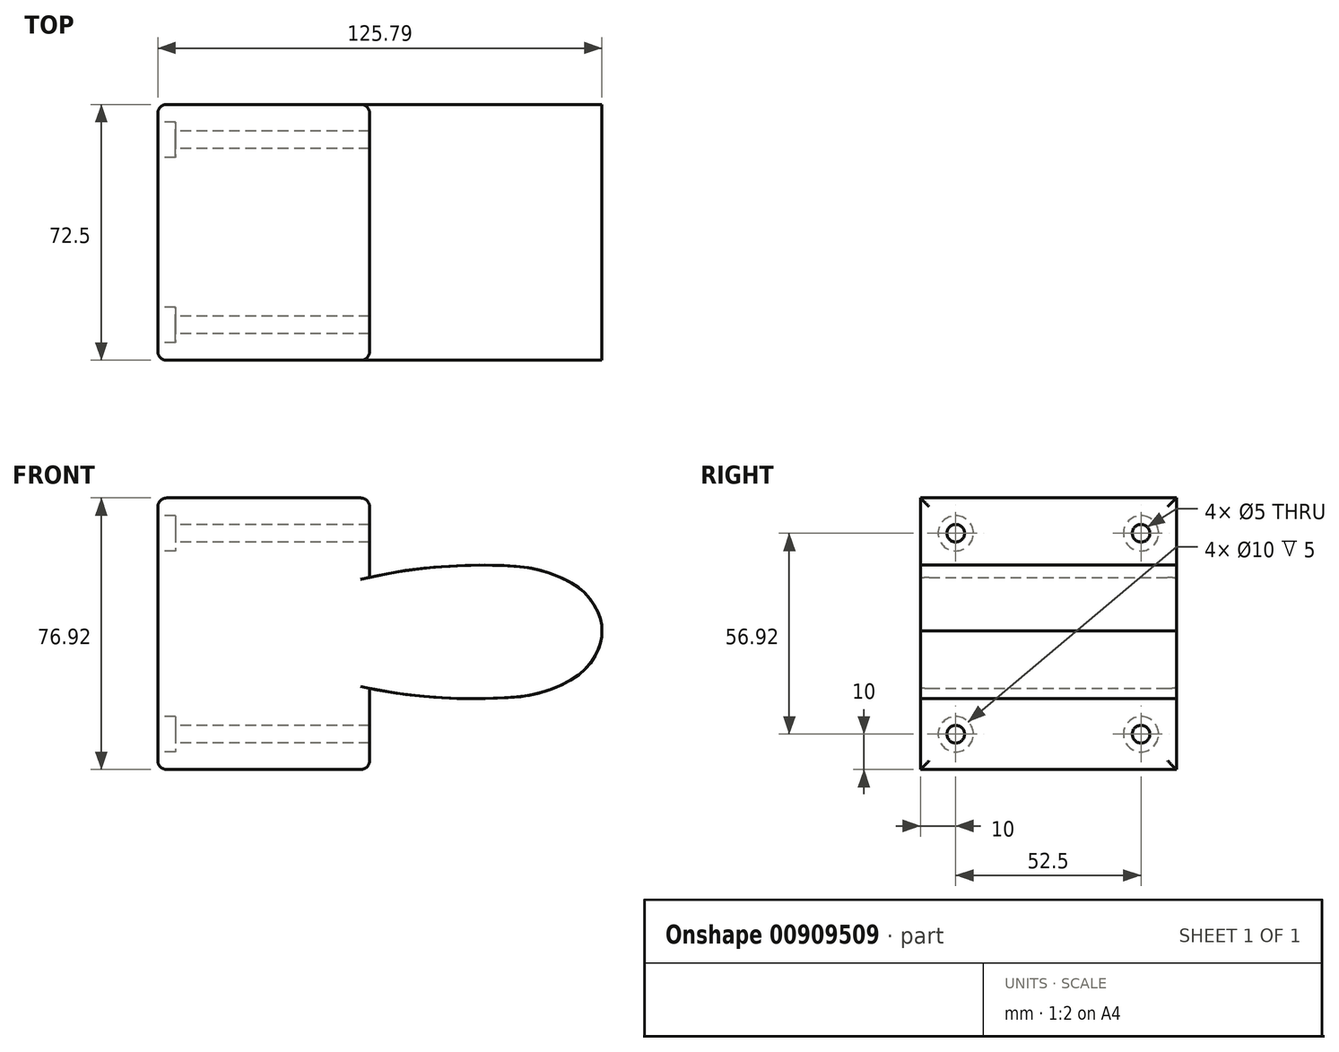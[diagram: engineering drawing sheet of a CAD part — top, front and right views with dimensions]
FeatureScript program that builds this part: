
annotation { "Feature Type Name" : "Feature", "Feature Type Description" : "" }
export const myFeature = defineFeature(function(context is Context, id is Id, definition is map)
    precondition{}
    {
        {
            var Q0;
            Q0=qCreatedBy(makeId("Front.planeOp"),FACE);
            var sketch = newSketch(context, id + "F0", { "sketchPlane" : qUnion([Q0])});
            skFitSpline(sketch, "E0.0", {"points": [v(-56.59, 0.04) * mm, v(-55.54, 0.85) * mm, v(-53.18, 2.44) * mm, v(-49, 4.79) * mm, v(-44.32, 7.05) * mm, v(-39.28, 9.2) * mm, v(-34.03, 11.2) * mm, v(-29.6, 12.7) * mm, v(-26.1, 13.78) * mm, v(-22.66, 14.76) * mm, v(-18.46, 15.83) * mm, v(-13.6, 16.88) * mm, v(-7.4, 18) * mm, v(-1.56, 18.74) * mm, v(3.83, 19.2) * mm, v(7.67, 19.44) * mm, v(11.33, 19.58) * mm, v(14.83, 19.62) * mm, v(17.61, 19.6) * mm, v(19.78, 19.56) * mm, v(21.92, 19.49) * mm, v(24.55, 19.33) * mm, v(27.14, 19.04) * mm, v(29.2, 18.69) * mm, v(30.73, 18.36) * mm, v(32.25, 17.95) * mm, v(34.23, 17.33) * mm, v(36.6, 16.42) * mm, v(38.75, 15.39) * mm, v(40.3, 14.52) * mm, v(41.36, 13.85) * mm, v(42.34, 13.16) * mm, v(43.26, 12.42) * mm, v(44.1, 11.62) * mm, v(44.9, 10.76) * mm, v(45.63, 9.83) * mm, v(46.32, 8.84) * mm, v(46.96, 7.8) * mm, v(47.53, 6.73) * mm, v(47.93, 5.84) * mm, v(48.2, 5.12) * mm, v(48.38, 4.58) * mm, v(48.52, 4.05) * mm, v(48.66, 3.37) * mm, v(48.77, 2.58) * mm, v(48.81, 1.73) * mm, v(48.82, 1.25) * mm, v(48.83, 1.03) * mm]});
            skFitSpline(sketch, "E0.1", {"points": [v(-56.59, 0.04) * mm, v(-55.52, -0.74) * mm, v(-53.13, -2.3) * mm, v(-48.9, -4.56) * mm, v(-44.19, -6.73) * mm, v(-39.1, -8.8) * mm, v(-33.82, -10.69) * mm, v(-29.36, -12.1) * mm, v(-25.85, -13.11) * mm, v(-22.38, -14.03) * mm, v(-18.17, -15.02) * mm, v(-13.3, -15.98) * mm, v(-7.06, -16.98) * mm, v(-1.22, -17.6) * mm, v(4.19, -17.98) * mm, v(8.03, -18.14) * mm, v(11.7, -18.2) * mm, v(15.19, -18.18) * mm, v(17.97, -18.1) * mm, v(20.13, -18.02) * mm, v(22.27, -17.91) * mm, v(24.9, -17.7) * mm, v(27.49, -17.36) * mm, v(29.54, -16.97) * mm, v(31.06, -16.62) * mm, v(32.57, -16.18) * mm, v(34.54, -15.52) * mm, v(36.9, -14.56) * mm, v(39.02, -13.5) * mm, v(40.55, -12.6) * mm, v(41.6, -11.9) * mm, v(42.58, -11.2) * mm, v(43.48, -10.44) * mm, v(44.3, -9.62) * mm, v(45.08, -8.75) * mm, v(45.8, -7.8) * mm, v(46.47, -6.8) * mm, v(47.09, -5.75) * mm, v(47.64, -4.67) * mm, v(48.02, -3.77) * mm, v(48.28, -3.05) * mm, v(48.45, -2.5) * mm, v(48.58, -1.97) * mm, v(48.7, -1.29) * mm, v(48.8, -0.5) * mm, v(48.83, 0.35) * mm, v(48.83, 0.83) * mm, v(48.83, 1.06) * mm]});
            skLineSegment(sketch, "E1", {"start": v(-16.96, 16.14) * mm, "end": v(-16.96, 38.67) * mm});
            skLineSegment(sketch, "E2", {"start": v(-16.96, 38.67) * mm, "end": v(-76.96, 38.67) * mm});
            skLineSegment(sketch, "E3", {"start": v(-76.96, 38.67) * mm, "end": v(-76.96, -38.25) * mm});
            skLineSegment(sketch, "E4", {"start": v(-76.96, -38.25) * mm, "end": v(-16.96, -38.25) * mm});
            skLineSegment(sketch, "E5", {"start": v(-16.96, -38.25) * mm, "end": v(-16.96, -15.25) * mm});
            skSolve(sketch);
        }
        {
            var Q0;
            Q0=qSketchRegion(id+"F0",true);
            extrude(context, id + "F1", {"entities" : qUnion([Q0]), "depth" : 72.5 * mm, "offsetDistance" : 25 * mm});
        }
        {
            var Q0;
            Q0=makeQuery(id+"F1.opExtrude","SWEPT_FACE",FACE,{"disambiguationData":[OSD([sQuery(id+"F0.wireOp",EDGE,"E3")])]});
            var sketch = newSketch(context, id + "F2", { "sketchPlane" : qUnion([Q0])});
            skLineSegment(sketch, "E6", {"start": v(10, 64.3) * mm, "end": v(10, -67.48) * mm, "construction": true});
            skLineSegment(sketch, "E7", {"start": v(62.5, 65.18) * mm, "end": v(62.5, -67.48) * mm, "construction": true});
            skLineSegment(sketch, "E8", {"start": v(-71.51, -28.25) * mm, "end": v(121.85, -28.25) * mm, "construction": true});
            skLineSegment(sketch, "E9", {"start": v(-71.51, 28.67) * mm, "end": v(123.4, 28.67) * mm, "construction": true});
            skPoint(sketch, "E10", {"position": v(10, 28.67) * mm});
            skPoint(sketch, "E11", {"position": v(62.5, 28.67) * mm});
            skPoint(sketch, "E12", {"position": v(62.5, -28.25) * mm});
            skPoint(sketch, "E13", {"position": v(10, -28.25) * mm});
            skSolve(sketch);
        }
        {
            var Q0;
            Q0=sQuery(id+"F2.wireOp",VERTEX,"E10");
            var Q1;
            Q1=sQuery(id+"F2.wireOp",VERTEX,"E11");
            var Q2;
            Q2=sQuery(id+"F2.wireOp",VERTEX,"E12");
            var Q3;
            Q3=sQuery(id+"F2.wireOp",VERTEX,"E13");
            var Q4;
            Q4=makeQuery(id+"F1.opExtrude","SWEPT_BODY",BODY,{"disambiguationData":[OSD([sQuery(id+"F0.wireOp",EDGE,"E0.0"),sQuery(id+"F0.wireOp",EDGE,"E0.1"),sQuery(id+"F0.wireOp",EDGE,"E1"),sQuery(id+"F0.wireOp",EDGE,"E2"),sQuery(id+"F0.wireOp",EDGE,"E3"),sQuery(id+"F0.wireOp",EDGE,"E4"),sQuery(id+"F0.wireOp",EDGE,"E5")])]});
            hole(context, id + "F3", {"style" : HoleStyle.C_BORE, "endStyle" : HoleEndStyle.THROUGH, "holeDiameter" : 5 * mm, "cBoreDiameter" : 10 * mm, "cBoreDepth" : 5 * mm, "majorDiameter" : 5 * mm, "isTappedThrough" : true, "tappedDepth" : 12 * mm, "tapClearance" : 3, "locations" : qUnion([Q0, Q1, Q2, Q3]), "scope" : qUnion([Q4])});
        }
        {
            var Q0;
            Q0=makeQuery(id+"F1.opExtrude","CAP_EDGE",EDGE,{"disambiguationData":[OSD([sQuery(id+"F0.wireOp",EDGE,"E3")])],"isStart":false});
            var Q1;
            Q1=makeQuery(id+"F1.opExtrude","SWEPT_EDGE",EDGE,{"disambiguationData":[OSD([sQuery(id+"F0.wireOp",EDGE,"E2"),sQuery(id+"F0.wireOp",EDGE,"E3")])]});
            var Q2;
            Q2=makeQuery(id+"F1.opExtrude","CAP_EDGE",EDGE,{"disambiguationData":[OSD([sQuery(id+"F0.wireOp",EDGE,"E3")])],"isStart":true});
            var Q3;
            Q3=makeQuery(id+"F1.opExtrude","SWEPT_EDGE",EDGE,{"disambiguationData":[OSD([sQuery(id+"F0.wireOp",EDGE,"E3"),sQuery(id+"F0.wireOp",EDGE,"E4")])]});
            fillet(context, id + "F4", {"entities" : qUnion([Q0, Q1, Q2, Q3]), "radius" : 2.5 * mm, "tangentPropagation" : true, "allowEdgeOverflow" : false});
        }
        {
            var Q0;
            Q0=makeQuery(id+"F1.opExtrude","SWEPT_EDGE",EDGE,{"disambiguationData":[OSD([sQuery(id+"F0.wireOp",EDGE,"E1"),sQuery(id+"F0.wireOp",EDGE,"E2")])]});
            var Q1;
            Q1=makeQuery(id+"F1.opExtrude","CAP_EDGE",EDGE,{"disambiguationData":[OSD([sQuery(id+"F0.wireOp",EDGE,"E1")])],"isStart":false});
            var Q2;
            Q2=makeQuery(id+"F1.opExtrude","CAP_EDGE",EDGE,{"disambiguationData":[OSD([sQuery(id+"F0.wireOp",EDGE,"E1")])],"isStart":true});
            var Q3;
            Q3=makeQuery(id+"F1.opExtrude","CAP_EDGE",EDGE,{"disambiguationData":[OSD([sQuery(id+"F0.wireOp",EDGE,"E5")])],"isStart":true});
            var Q4;
            Q4=makeQuery(id+"F1.opExtrude","SWEPT_EDGE",EDGE,{"disambiguationData":[OSD([sQuery(id+"F0.wireOp",EDGE,"E4"),sQuery(id+"F0.wireOp",EDGE,"E5")])]});
            var Q5;
            Q5=makeQuery(id+"F1.opExtrude","CAP_EDGE",EDGE,{"disambiguationData":[OSD([sQuery(id+"F0.wireOp",EDGE,"E5")])],"isStart":false});
            fillet(context, id + "F5", {"entities" : qUnion([Q0, Q1, Q2, Q3, Q4, Q5]), "radius" : 2.5 * mm, "tangentPropagation" : true, "allowEdgeOverflow" : false});
        }
    });
